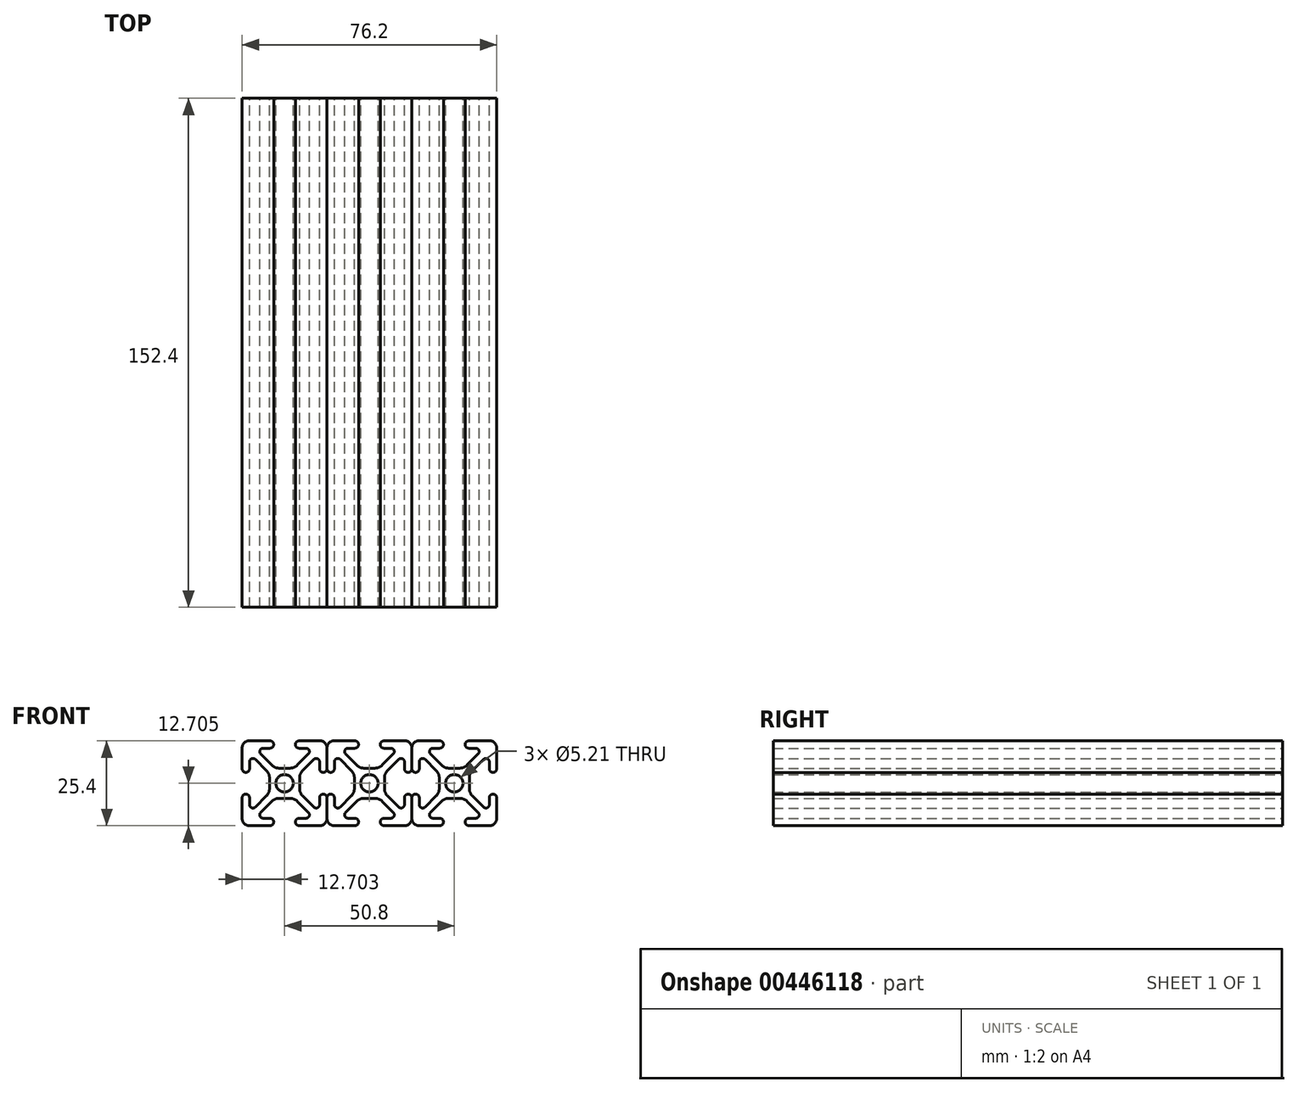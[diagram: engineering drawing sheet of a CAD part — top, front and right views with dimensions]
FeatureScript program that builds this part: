
annotation { "Feature Type Name" : "Feature", "Feature Type Description" : "" }
export const myFeature = defineFeature(function(context is Context, id is Id, definition is map)
    precondition{}
    {
        {
            var Q0;
            Q0=qCreatedBy(makeId("Front.planeOp"),FACE);
            var sketch = newSketch(context, id + "F0", { "sketchPlane" : qUnion([Q0])});
            skArc(sketch, "E0", {"start": v(-10.62, 12.76) * mm, "mid": v(-12.1, 12.15) * mm, "end": v(-12.73, 10.66) * mm});
            skArc(sketch, "E1", {"start": v(-12.73, 4.4) * mm, "mid": v(-11.62, 3.3) * mm, "end": v(-10.52, 4.4) * mm});
            skArc(sketch, "E2", {"start": v(-4.37, 10.55) * mm, "mid": v(-3.27, 11.66) * mm, "end": v(-4.37, 12.76) * mm});
            skArc(sketch, "E3", {"start": v(-8.75, 7.2) * mm, "mid": v(-9.88, 7.42) * mm, "end": v(-10.52, 6.46) * mm});
            skArc(sketch, "E4", {"start": v(-6.43, 10.55) * mm, "mid": v(-7.38, 9.92) * mm, "end": v(-7.16, 8.8) * mm});
            skLineSegment(sketch, "E5", {"start": v(-12.73, 10.66) * mm, "end": v(-12.73, 4.4) * mm});
            skLineSegment(sketch, "E6", {"start": v(-10.62, 12.76) * mm, "end": v(-4.37, 12.76) * mm});
            skLineSegment(sketch, "E7", {"start": v(-10.52, 4.4) * mm, "end": v(-10.52, 6.46) * mm});
            skLineSegment(sketch, "E8", {"start": v(-4.37, 10.55) * mm, "end": v(-6.43, 10.55) * mm});
            skLineSegment(sketch, "E9", {"start": v(-11.51, 7.5) * mm, "end": v(-10.3, 7.5) * mm, "construction": true});
            skLineSegment(sketch, "E10", {"start": v(-13.64, 3.3) * mm, "end": v(-12.36, 3.3) * mm, "construction": true});
            skLineSegment(sketch, "E11", {"start": v(-7.46, 11.03) * mm, "end": v(-7.46, 8.91) * mm, "construction": true});
            skLineSegment(sketch, "E12", {"start": v(-3.27, 12.37) * mm, "end": v(-3.27, 10.25) * mm, "construction": true});
            skLineSegment(sketch, "E13.bottom", {"start": v(1.57, 4.57) * mm, "end": v(-1.63, 4.57) * mm});
            skLineSegment(sketch, "E13.top", {"start": v(1.57, -4.44) * mm, "end": v(-1.63, -4.44) * mm});
            skLineSegment(sketch, "E13.left", {"start": v(4.48, 1.66) * mm, "end": v(4.48, -1.53) * mm});
            skLineSegment(sketch, "E13.right", {"start": v(-4.54, 1.66) * mm, "end": v(-4.54, -1.53) * mm});
            skPoint(sketch, "E13.middle", {"position": v(-0.03, 0.06) * mm});
            skLineSegment(sketch, "E14", {"start": v(-8.75, 7.2) * mm, "end": v(-5.47, 3.9) * mm});
            skLineSegment(sketch, "E15", {"start": v(-7.16, 8.8) * mm, "end": v(-3.87, 5.5) * mm});
            skArc(sketch, "E16.filletArc", {"start": v(-3.87, 5.5) * mm, "mid": v(-2.84, 4.81) * mm, "end": v(-1.63, 4.57) * mm});
            skArc(sketch, "E17.filletArc", {"start": v(-4.54, 1.66) * mm, "mid": v(-4.78, 2.88) * mm, "end": v(-5.47, 3.9) * mm});
            skLineSegment(sketch, "E18", {"start": v(5.32, 0.06) * mm, "end": v(-7.21, 0.06) * mm, "construction": true});
            skPoint(sketch, "E18.startSnap0", {"position": v(2.97, 0.06) * mm});
            skPoint(sketch, "E19", {"position": v(-0.03, -4.44) * mm});
            skLineSegment(sketch, "E20", {"start": v(-0.03, -6.76) * mm, "end": v(-0.03, 5.83) * mm, "construction": true});
            skLineSegment(sketch, "E21.MirrorCS", {"start": v(11.46, 7.5) * mm, "end": v(10.25, 7.5) * mm, "construction": true});
            skArc(sketch, "E22.MirrorCS", {"start": v(10.57, 12.76) * mm, "mid": v(12.06, 12.15) * mm, "end": v(12.67, 10.66) * mm});
            skLineSegment(sketch, "E23.MirrorCS", {"start": v(7.4, 11.03) * mm, "end": v(7.4, 8.91) * mm, "construction": true});
            skLineSegment(sketch, "E24.MirrorCS", {"start": v(10.46, 4.4) * mm, "end": v(10.46, 6.46) * mm});
            skArc(sketch, "E25.MirrorCS", {"start": v(3.82, 5.5) * mm, "mid": v(2.79, 4.81) * mm, "end": v(1.57, 4.57) * mm});
            skLineSegment(sketch, "E26.MirrorCS", {"start": v(8.7, 7.2) * mm, "end": v(5.41, 3.9) * mm});
            skLineSegment(sketch, "E27.MirrorCS", {"start": v(3.21, 12.37) * mm, "end": v(3.21, 10.25) * mm, "construction": true});
            skLineSegment(sketch, "E28.MirrorCS", {"start": v(13.58, 3.3) * mm, "end": v(12.3, 3.3) * mm, "construction": true});
            skArc(sketch, "E29.MirrorCS", {"start": v(4.32, 10.55) * mm, "mid": v(3.21, 11.66) * mm, "end": v(4.32, 12.76) * mm});
            skArc(sketch, "E30.MirrorCS", {"start": v(8.7, 7.2) * mm, "mid": v(9.83, 7.42) * mm, "end": v(10.46, 6.46) * mm});
            skArc(sketch, "E31.MirrorCS", {"start": v(12.67, 4.4) * mm, "mid": v(11.57, 3.3) * mm, "end": v(10.46, 4.4) * mm});
            skLineSegment(sketch, "E32.MirrorCS", {"start": v(10.57, 12.76) * mm, "end": v(4.32, 12.76) * mm});
            skLineSegment(sketch, "E33.MirrorCS", {"start": v(12.67, 10.66) * mm, "end": v(12.67, 4.4) * mm});
            skArc(sketch, "E34.MirrorCS", {"start": v(6.37, 10.55) * mm, "mid": v(7.33, 9.92) * mm, "end": v(7.1, 8.8) * mm});
            skLineSegment(sketch, "E35.MirrorCS", {"start": v(7.1, 8.8) * mm, "end": v(3.82, 5.5) * mm});
            skLineSegment(sketch, "E36.MirrorCS", {"start": v(4.32, 10.55) * mm, "end": v(6.37, 10.55) * mm});
            skArc(sketch, "E37.MirrorCS", {"start": v(4.48, 1.66) * mm, "mid": v(4.72, 2.88) * mm, "end": v(5.41, 3.9) * mm});
            skLineSegment(sketch, "E38.MirrorCS", {"start": v(-11.51, -7.37) * mm, "end": v(-10.3, -7.37) * mm, "construction": true});
            skArc(sketch, "E39.MirrorCS", {"start": v(-3.87, -5.37) * mm, "mid": v(-2.84, -4.69) * mm, "end": v(-1.63, -4.44) * mm});
            skArc(sketch, "E40.MirrorCS", {"start": v(-10.62, -12.64) * mm, "mid": v(-12.1, -12.02) * mm, "end": v(-12.73, -10.53) * mm});
            skArc(sketch, "E41.MirrorCS", {"start": v(-8.75, -7.07) * mm, "mid": v(-9.88, -7.3) * mm, "end": v(-10.52, -6.33) * mm});
            skArc(sketch, "E42.MirrorCS", {"start": v(-6.43, -10.43) * mm, "mid": v(-7.38, -9.79) * mm, "end": v(-7.16, -8.66) * mm});
            skLineSegment(sketch, "E43.MirrorCS", {"start": v(-3.27, -12.24) * mm, "end": v(-3.27, -10.12) * mm, "construction": true});
            skArc(sketch, "E44.MirrorCS", {"start": v(-4.54, -1.53) * mm, "mid": v(-4.78, -2.75) * mm, "end": v(-5.47, -3.78) * mm});
            skLineSegment(sketch, "E45.MirrorCS", {"start": v(-12.73, -10.53) * mm, "end": v(-12.73, -4.28) * mm});
            skLineSegment(sketch, "E46.MirrorCS", {"start": v(-13.64, -3.17) * mm, "end": v(-12.36, -3.17) * mm, "construction": true});
            skLineSegment(sketch, "E47.MirrorCS", {"start": v(-7.46, -10.9) * mm, "end": v(-7.46, -8.78) * mm, "construction": true});
            skLineSegment(sketch, "E48.MirrorCS", {"start": v(-4.37, -10.43) * mm, "end": v(-6.43, -10.43) * mm});
            skLineSegment(sketch, "E49.MirrorCS", {"start": v(-10.62, -12.64) * mm, "end": v(-4.37, -12.64) * mm});
            skLineSegment(sketch, "E50.MirrorCS", {"start": v(-10.52, -4.28) * mm, "end": v(-10.52, -6.33) * mm});
            skArc(sketch, "E51.MirrorCS", {"start": v(-12.73, -4.28) * mm, "mid": v(-11.62, -3.17) * mm, "end": v(-10.52, -4.28) * mm});
            skLineSegment(sketch, "E52.MirrorCS", {"start": v(-8.75, -7.07) * mm, "end": v(-5.47, -3.78) * mm});
            skLineSegment(sketch, "E53.MirrorCS", {"start": v(-7.16, -8.66) * mm, "end": v(-3.87, -5.37) * mm});
            skArc(sketch, "E54.MirrorCS", {"start": v(-4.37, -10.43) * mm, "mid": v(-3.27, -11.53) * mm, "end": v(-4.37, -12.64) * mm});
            skLineSegment(sketch, "E55.MirrorCS", {"start": v(11.46, -7.37) * mm, "end": v(10.25, -7.37) * mm, "construction": true});
            skArc(sketch, "E56.MirrorCS", {"start": v(4.32, -10.43) * mm, "mid": v(3.21, -11.53) * mm, "end": v(4.32, -12.64) * mm});
            skLineSegment(sketch, "E57.MirrorCS", {"start": v(13.58, -3.17) * mm, "end": v(12.3, -3.17) * mm, "construction": true});
            skArc(sketch, "E58.MirrorCS", {"start": v(8.7, -7.07) * mm, "mid": v(9.83, -7.3) * mm, "end": v(10.46, -6.33) * mm});
            skLineSegment(sketch, "E59.MirrorCS", {"start": v(7.1, -8.66) * mm, "end": v(3.82, -5.37) * mm});
            skLineSegment(sketch, "E60.MirrorCS", {"start": v(7.4, -10.9) * mm, "end": v(7.4, -8.78) * mm, "construction": true});
            skLineSegment(sketch, "E61.MirrorCS", {"start": v(3.21, -12.24) * mm, "end": v(3.21, -10.12) * mm, "construction": true});
            skLineSegment(sketch, "E62.MirrorCS", {"start": v(4.32, -10.43) * mm, "end": v(6.37, -10.43) * mm});
            skArc(sketch, "E63.MirrorCS", {"start": v(3.82, -5.37) * mm, "mid": v(2.79, -4.69) * mm, "end": v(1.57, -4.44) * mm});
            skArc(sketch, "E64.MirrorCS", {"start": v(10.57, -12.64) * mm, "mid": v(12.06, -12.02) * mm, "end": v(12.67, -10.53) * mm});
            skLineSegment(sketch, "E65.MirrorCS", {"start": v(10.57, -12.64) * mm, "end": v(4.32, -12.64) * mm});
            skLineSegment(sketch, "E66.MirrorCS", {"start": v(8.7, -7.07) * mm, "end": v(5.41, -3.78) * mm});
            skLineSegment(sketch, "E67.MirrorCS", {"start": v(12.67, -10.53) * mm, "end": v(12.67, -4.28) * mm});
            skArc(sketch, "E68.MirrorCS", {"start": v(12.67, -4.28) * mm, "mid": v(11.57, -3.17) * mm, "end": v(10.46, -4.28) * mm});
            skArc(sketch, "E69.MirrorCS", {"start": v(4.48, -1.53) * mm, "mid": v(4.72, -2.75) * mm, "end": v(5.41, -3.78) * mm});
            skLineSegment(sketch, "E70.MirrorCS", {"start": v(10.46, -4.28) * mm, "end": v(10.46, -6.33) * mm});
            skArc(sketch, "E71.MirrorCS", {"start": v(6.37, -10.43) * mm, "mid": v(7.33, -9.79) * mm, "end": v(7.1, -8.66) * mm});
            skCircle(sketch, "E72", {"center": v(-0.03, 0.06) * mm, "radius": 2.6 * mm});
            skSolve(sketch);
        }
        {
            var Q0;
            Q0=qSketchRegion(id+"F0",true);
            extrude(context, id + "F1", {"entities" : qUnion([Q0]), "depth" : 152.4 * mm});
        }
        {
            var Q0;
            Q0=makeQuery(id+"F1.opExtrude","SWEPT_BODY",BODY,{"disambiguationData":[OSD([sQuery(id+"F0.wireOp",EDGE,"E0"),sQuery(id+"F0.wireOp",EDGE,"E1"),sQuery(id+"F0.wireOp",EDGE,"E2"),sQuery(id+"F0.wireOp",EDGE,"E3"),sQuery(id+"F0.wireOp",EDGE,"E4"),sQuery(id+"F0.wireOp",EDGE,"E5"),sQuery(id+"F0.wireOp",EDGE,"E6"),sQuery(id+"F0.wireOp",EDGE,"E7"),sQuery(id+"F0.wireOp",EDGE,"E8"),sQuery(id+"F0.wireOp",EDGE,"E13.bottom"),sQuery(id+"F0.wireOp",EDGE,"E13.top"),sQuery(id+"F0.wireOp",EDGE,"E13.left"),sQuery(id+"F0.wireOp",EDGE,"E13.right"),sQuery(id+"F0.wireOp",EDGE,"E14"),sQuery(id+"F0.wireOp",EDGE,"E15"),sQuery(id+"F0.wireOp",EDGE,"E16.filletArc"),sQuery(id+"F0.wireOp",EDGE,"E17.filletArc"),sQuery(id+"F0.wireOp",EDGE,"E22.MirrorCS"),sQuery(id+"F0.wireOp",EDGE,"E24.MirrorCS"),sQuery(id+"F0.wireOp",EDGE,"E25.MirrorCS"),sQuery(id+"F0.wireOp",EDGE,"E26.MirrorCS"),sQuery(id+"F0.wireOp",EDGE,"E29.MirrorCS"),sQuery(id+"F0.wireOp",EDGE,"E30.MirrorCS"),sQuery(id+"F0.wireOp",EDGE,"E31.MirrorCS"),sQuery(id+"F0.wireOp",EDGE,"E32.MirrorCS"),sQuery(id+"F0.wireOp",EDGE,"E33.MirrorCS"),sQuery(id+"F0.wireOp",EDGE,"E34.MirrorCS"),sQuery(id+"F0.wireOp",EDGE,"E35.MirrorCS"),sQuery(id+"F0.wireOp",EDGE,"E36.MirrorCS"),sQuery(id+"F0.wireOp",EDGE,"E37.MirrorCS"),sQuery(id+"F0.wireOp",EDGE,"E39.MirrorCS"),sQuery(id+"F0.wireOp",EDGE,"E40.MirrorCS"),sQuery(id+"F0.wireOp",EDGE,"E41.MirrorCS"),sQuery(id+"F0.wireOp",EDGE,"E42.MirrorCS"),sQuery(id+"F0.wireOp",EDGE,"E44.MirrorCS"),sQuery(id+"F0.wireOp",EDGE,"E45.MirrorCS"),sQuery(id+"F0.wireOp",EDGE,"E48.MirrorCS"),sQuery(id+"F0.wireOp",EDGE,"E49.MirrorCS"),sQuery(id+"F0.wireOp",EDGE,"E50.MirrorCS"),sQuery(id+"F0.wireOp",EDGE,"E51.MirrorCS"),sQuery(id+"F0.wireOp",EDGE,"E52.MirrorCS"),sQuery(id+"F0.wireOp",EDGE,"E53.MirrorCS"),sQuery(id+"F0.wireOp",EDGE,"E54.MirrorCS"),sQuery(id+"F0.wireOp",EDGE,"E56.MirrorCS"),sQuery(id+"F0.wireOp",EDGE,"E58.MirrorCS"),sQuery(id+"F0.wireOp",EDGE,"E59.MirrorCS"),sQuery(id+"F0.wireOp",EDGE,"E62.MirrorCS"),sQuery(id+"F0.wireOp",EDGE,"E63.MirrorCS"),sQuery(id+"F0.wireOp",EDGE,"E64.MirrorCS"),sQuery(id+"F0.wireOp",EDGE,"E65.MirrorCS"),sQuery(id+"F0.wireOp",EDGE,"E66.MirrorCS"),sQuery(id+"F0.wireOp",EDGE,"E67.MirrorCS"),sQuery(id+"F0.wireOp",EDGE,"E68.MirrorCS"),sQuery(id+"F0.wireOp",EDGE,"E69.MirrorCS"),sQuery(id+"F0.wireOp",EDGE,"E70.MirrorCS"),sQuery(id+"F0.wireOp",EDGE,"E71.MirrorCS"),sQuery(id+"F0.wireOp",EDGE,"E72")])]});
            transform(context, id + "F2", {"entities" : qUnion([Q0]), "transformType" : TransformType.TRANSLATION_3D, "dx" : 0 * mm, "dy" : 0 * mm, "dz" : 0 * mm, "makeCopy" : true});
        }
        {
            var Q0;
            Q0=makeQuery(id+"F2.opPattern","COPY",BODY,{"derivedFrom":makeQuery(id+"F1.opExtrude","SWEPT_BODY",BODY,{"disambiguationData":[OSD([sQuery(id+"F0.wireOp",EDGE,"E0"),sQuery(id+"F0.wireOp",EDGE,"E1"),sQuery(id+"F0.wireOp",EDGE,"E2"),sQuery(id+"F0.wireOp",EDGE,"E3"),sQuery(id+"F0.wireOp",EDGE,"E4"),sQuery(id+"F0.wireOp",EDGE,"E5"),sQuery(id+"F0.wireOp",EDGE,"E6"),sQuery(id+"F0.wireOp",EDGE,"E7"),sQuery(id+"F0.wireOp",EDGE,"E8"),sQuery(id+"F0.wireOp",EDGE,"E13.bottom"),sQuery(id+"F0.wireOp",EDGE,"E13.top"),sQuery(id+"F0.wireOp",EDGE,"E13.left"),sQuery(id+"F0.wireOp",EDGE,"E13.right"),sQuery(id+"F0.wireOp",EDGE,"E14"),sQuery(id+"F0.wireOp",EDGE,"E15"),sQuery(id+"F0.wireOp",EDGE,"E16.filletArc"),sQuery(id+"F0.wireOp",EDGE,"E17.filletArc"),sQuery(id+"F0.wireOp",EDGE,"E22.MirrorCS"),sQuery(id+"F0.wireOp",EDGE,"E24.MirrorCS"),sQuery(id+"F0.wireOp",EDGE,"E25.MirrorCS"),sQuery(id+"F0.wireOp",EDGE,"E26.MirrorCS"),sQuery(id+"F0.wireOp",EDGE,"E29.MirrorCS"),sQuery(id+"F0.wireOp",EDGE,"E30.MirrorCS"),sQuery(id+"F0.wireOp",EDGE,"E31.MirrorCS"),sQuery(id+"F0.wireOp",EDGE,"E32.MirrorCS"),sQuery(id+"F0.wireOp",EDGE,"E33.MirrorCS"),sQuery(id+"F0.wireOp",EDGE,"E34.MirrorCS"),sQuery(id+"F0.wireOp",EDGE,"E35.MirrorCS"),sQuery(id+"F0.wireOp",EDGE,"E36.MirrorCS"),sQuery(id+"F0.wireOp",EDGE,"E37.MirrorCS"),sQuery(id+"F0.wireOp",EDGE,"E39.MirrorCS"),sQuery(id+"F0.wireOp",EDGE,"E40.MirrorCS"),sQuery(id+"F0.wireOp",EDGE,"E41.MirrorCS"),sQuery(id+"F0.wireOp",EDGE,"E42.MirrorCS"),sQuery(id+"F0.wireOp",EDGE,"E44.MirrorCS"),sQuery(id+"F0.wireOp",EDGE,"E45.MirrorCS"),sQuery(id+"F0.wireOp",EDGE,"E48.MirrorCS"),sQuery(id+"F0.wireOp",EDGE,"E49.MirrorCS"),sQuery(id+"F0.wireOp",EDGE,"E50.MirrorCS"),sQuery(id+"F0.wireOp",EDGE,"E51.MirrorCS"),sQuery(id+"F0.wireOp",EDGE,"E52.MirrorCS"),sQuery(id+"F0.wireOp",EDGE,"E53.MirrorCS"),sQuery(id+"F0.wireOp",EDGE,"E54.MirrorCS"),sQuery(id+"F0.wireOp",EDGE,"E56.MirrorCS"),sQuery(id+"F0.wireOp",EDGE,"E58.MirrorCS"),sQuery(id+"F0.wireOp",EDGE,"E59.MirrorCS"),sQuery(id+"F0.wireOp",EDGE,"E62.MirrorCS"),sQuery(id+"F0.wireOp",EDGE,"E63.MirrorCS"),sQuery(id+"F0.wireOp",EDGE,"E64.MirrorCS"),sQuery(id+"F0.wireOp",EDGE,"E65.MirrorCS"),sQuery(id+"F0.wireOp",EDGE,"E66.MirrorCS"),sQuery(id+"F0.wireOp",EDGE,"E67.MirrorCS"),sQuery(id+"F0.wireOp",EDGE,"E68.MirrorCS"),sQuery(id+"F0.wireOp",EDGE,"E69.MirrorCS"),sQuery(id+"F0.wireOp",EDGE,"E70.MirrorCS"),sQuery(id+"F0.wireOp",EDGE,"E71.MirrorCS"),sQuery(id+"F0.wireOp",EDGE,"E72")])]}),"instanceName":"1"});
            deleteBodies(context, id + "F3", {"entities" : qUnion([Q0])});
        }
        {
            var Q0;
            Q0=makeQuery(id+"F1.opExtrude","SWEPT_BODY",BODY,{"disambiguationData":[OSD([sQuery(id+"F0.wireOp",EDGE,"E0"),sQuery(id+"F0.wireOp",EDGE,"E1"),sQuery(id+"F0.wireOp",EDGE,"E2"),sQuery(id+"F0.wireOp",EDGE,"E3"),sQuery(id+"F0.wireOp",EDGE,"E4"),sQuery(id+"F0.wireOp",EDGE,"E5"),sQuery(id+"F0.wireOp",EDGE,"E6"),sQuery(id+"F0.wireOp",EDGE,"E7"),sQuery(id+"F0.wireOp",EDGE,"E8"),sQuery(id+"F0.wireOp",EDGE,"E13.bottom"),sQuery(id+"F0.wireOp",EDGE,"E13.top"),sQuery(id+"F0.wireOp",EDGE,"E13.left"),sQuery(id+"F0.wireOp",EDGE,"E13.right"),sQuery(id+"F0.wireOp",EDGE,"E14"),sQuery(id+"F0.wireOp",EDGE,"E15"),sQuery(id+"F0.wireOp",EDGE,"E16.filletArc"),sQuery(id+"F0.wireOp",EDGE,"E17.filletArc"),sQuery(id+"F0.wireOp",EDGE,"E22.MirrorCS"),sQuery(id+"F0.wireOp",EDGE,"E24.MirrorCS"),sQuery(id+"F0.wireOp",EDGE,"E25.MirrorCS"),sQuery(id+"F0.wireOp",EDGE,"E26.MirrorCS"),sQuery(id+"F0.wireOp",EDGE,"E29.MirrorCS"),sQuery(id+"F0.wireOp",EDGE,"E30.MirrorCS"),sQuery(id+"F0.wireOp",EDGE,"E31.MirrorCS"),sQuery(id+"F0.wireOp",EDGE,"E32.MirrorCS"),sQuery(id+"F0.wireOp",EDGE,"E33.MirrorCS"),sQuery(id+"F0.wireOp",EDGE,"E34.MirrorCS"),sQuery(id+"F0.wireOp",EDGE,"E35.MirrorCS"),sQuery(id+"F0.wireOp",EDGE,"E36.MirrorCS"),sQuery(id+"F0.wireOp",EDGE,"E37.MirrorCS"),sQuery(id+"F0.wireOp",EDGE,"E39.MirrorCS"),sQuery(id+"F0.wireOp",EDGE,"E40.MirrorCS"),sQuery(id+"F0.wireOp",EDGE,"E41.MirrorCS"),sQuery(id+"F0.wireOp",EDGE,"E42.MirrorCS"),sQuery(id+"F0.wireOp",EDGE,"E44.MirrorCS"),sQuery(id+"F0.wireOp",EDGE,"E45.MirrorCS"),sQuery(id+"F0.wireOp",EDGE,"E48.MirrorCS"),sQuery(id+"F0.wireOp",EDGE,"E49.MirrorCS"),sQuery(id+"F0.wireOp",EDGE,"E50.MirrorCS"),sQuery(id+"F0.wireOp",EDGE,"E51.MirrorCS"),sQuery(id+"F0.wireOp",EDGE,"E52.MirrorCS"),sQuery(id+"F0.wireOp",EDGE,"E53.MirrorCS"),sQuery(id+"F0.wireOp",EDGE,"E54.MirrorCS"),sQuery(id+"F0.wireOp",EDGE,"E56.MirrorCS"),sQuery(id+"F0.wireOp",EDGE,"E58.MirrorCS"),sQuery(id+"F0.wireOp",EDGE,"E59.MirrorCS"),sQuery(id+"F0.wireOp",EDGE,"E62.MirrorCS"),sQuery(id+"F0.wireOp",EDGE,"E63.MirrorCS"),sQuery(id+"F0.wireOp",EDGE,"E64.MirrorCS"),sQuery(id+"F0.wireOp",EDGE,"E65.MirrorCS"),sQuery(id+"F0.wireOp",EDGE,"E66.MirrorCS"),sQuery(id+"F0.wireOp",EDGE,"E67.MirrorCS"),sQuery(id+"F0.wireOp",EDGE,"E68.MirrorCS"),sQuery(id+"F0.wireOp",EDGE,"E69.MirrorCS"),sQuery(id+"F0.wireOp",EDGE,"E70.MirrorCS"),sQuery(id+"F0.wireOp",EDGE,"E71.MirrorCS"),sQuery(id+"F0.wireOp",EDGE,"E72")])]});
            transform(context, id + "F4", {"entities" : qUnion([Q0]), "transformType" : TransformType.TRANSLATION_3D, "dx" : 25.4 * mm, "dy" : 0 * mm, "dz" : 0 * mm, "makeCopy" : true});
        }
        {
            var Q0;
            Q0=makeQuery(id+"F1.opExtrude","SWEPT_BODY",BODY,{"disambiguationData":[OSD([sQuery(id+"F0.wireOp",EDGE,"E0"),sQuery(id+"F0.wireOp",EDGE,"E1"),sQuery(id+"F0.wireOp",EDGE,"E2"),sQuery(id+"F0.wireOp",EDGE,"E3"),sQuery(id+"F0.wireOp",EDGE,"E4"),sQuery(id+"F0.wireOp",EDGE,"E5"),sQuery(id+"F0.wireOp",EDGE,"E6"),sQuery(id+"F0.wireOp",EDGE,"E7"),sQuery(id+"F0.wireOp",EDGE,"E8"),sQuery(id+"F0.wireOp",EDGE,"E13.bottom"),sQuery(id+"F0.wireOp",EDGE,"E13.top"),sQuery(id+"F0.wireOp",EDGE,"E13.left"),sQuery(id+"F0.wireOp",EDGE,"E13.right"),sQuery(id+"F0.wireOp",EDGE,"E14"),sQuery(id+"F0.wireOp",EDGE,"E15"),sQuery(id+"F0.wireOp",EDGE,"E16.filletArc"),sQuery(id+"F0.wireOp",EDGE,"E17.filletArc"),sQuery(id+"F0.wireOp",EDGE,"E22.MirrorCS"),sQuery(id+"F0.wireOp",EDGE,"E24.MirrorCS"),sQuery(id+"F0.wireOp",EDGE,"E25.MirrorCS"),sQuery(id+"F0.wireOp",EDGE,"E26.MirrorCS"),sQuery(id+"F0.wireOp",EDGE,"E29.MirrorCS"),sQuery(id+"F0.wireOp",EDGE,"E30.MirrorCS"),sQuery(id+"F0.wireOp",EDGE,"E31.MirrorCS"),sQuery(id+"F0.wireOp",EDGE,"E32.MirrorCS"),sQuery(id+"F0.wireOp",EDGE,"E33.MirrorCS"),sQuery(id+"F0.wireOp",EDGE,"E34.MirrorCS"),sQuery(id+"F0.wireOp",EDGE,"E35.MirrorCS"),sQuery(id+"F0.wireOp",EDGE,"E36.MirrorCS"),sQuery(id+"F0.wireOp",EDGE,"E37.MirrorCS"),sQuery(id+"F0.wireOp",EDGE,"E39.MirrorCS"),sQuery(id+"F0.wireOp",EDGE,"E40.MirrorCS"),sQuery(id+"F0.wireOp",EDGE,"E41.MirrorCS"),sQuery(id+"F0.wireOp",EDGE,"E42.MirrorCS"),sQuery(id+"F0.wireOp",EDGE,"E44.MirrorCS"),sQuery(id+"F0.wireOp",EDGE,"E45.MirrorCS"),sQuery(id+"F0.wireOp",EDGE,"E48.MirrorCS"),sQuery(id+"F0.wireOp",EDGE,"E49.MirrorCS"),sQuery(id+"F0.wireOp",EDGE,"E50.MirrorCS"),sQuery(id+"F0.wireOp",EDGE,"E51.MirrorCS"),sQuery(id+"F0.wireOp",EDGE,"E52.MirrorCS"),sQuery(id+"F0.wireOp",EDGE,"E53.MirrorCS"),sQuery(id+"F0.wireOp",EDGE,"E54.MirrorCS"),sQuery(id+"F0.wireOp",EDGE,"E56.MirrorCS"),sQuery(id+"F0.wireOp",EDGE,"E58.MirrorCS"),sQuery(id+"F0.wireOp",EDGE,"E59.MirrorCS"),sQuery(id+"F0.wireOp",EDGE,"E62.MirrorCS"),sQuery(id+"F0.wireOp",EDGE,"E63.MirrorCS"),sQuery(id+"F0.wireOp",EDGE,"E64.MirrorCS"),sQuery(id+"F0.wireOp",EDGE,"E65.MirrorCS"),sQuery(id+"F0.wireOp",EDGE,"E66.MirrorCS"),sQuery(id+"F0.wireOp",EDGE,"E67.MirrorCS"),sQuery(id+"F0.wireOp",EDGE,"E68.MirrorCS"),sQuery(id+"F0.wireOp",EDGE,"E69.MirrorCS"),sQuery(id+"F0.wireOp",EDGE,"E70.MirrorCS"),sQuery(id+"F0.wireOp",EDGE,"E71.MirrorCS"),sQuery(id+"F0.wireOp",EDGE,"E72")])]});
            transform(context, id + "F5", {"entities" : qUnion([Q0]), "transformType" : TransformType.TRANSLATION_3D, "dx" : -25.4 * mm, "dy" : 0 * mm, "dz" : 0 * mm, "makeCopy" : true});
        }
    });
